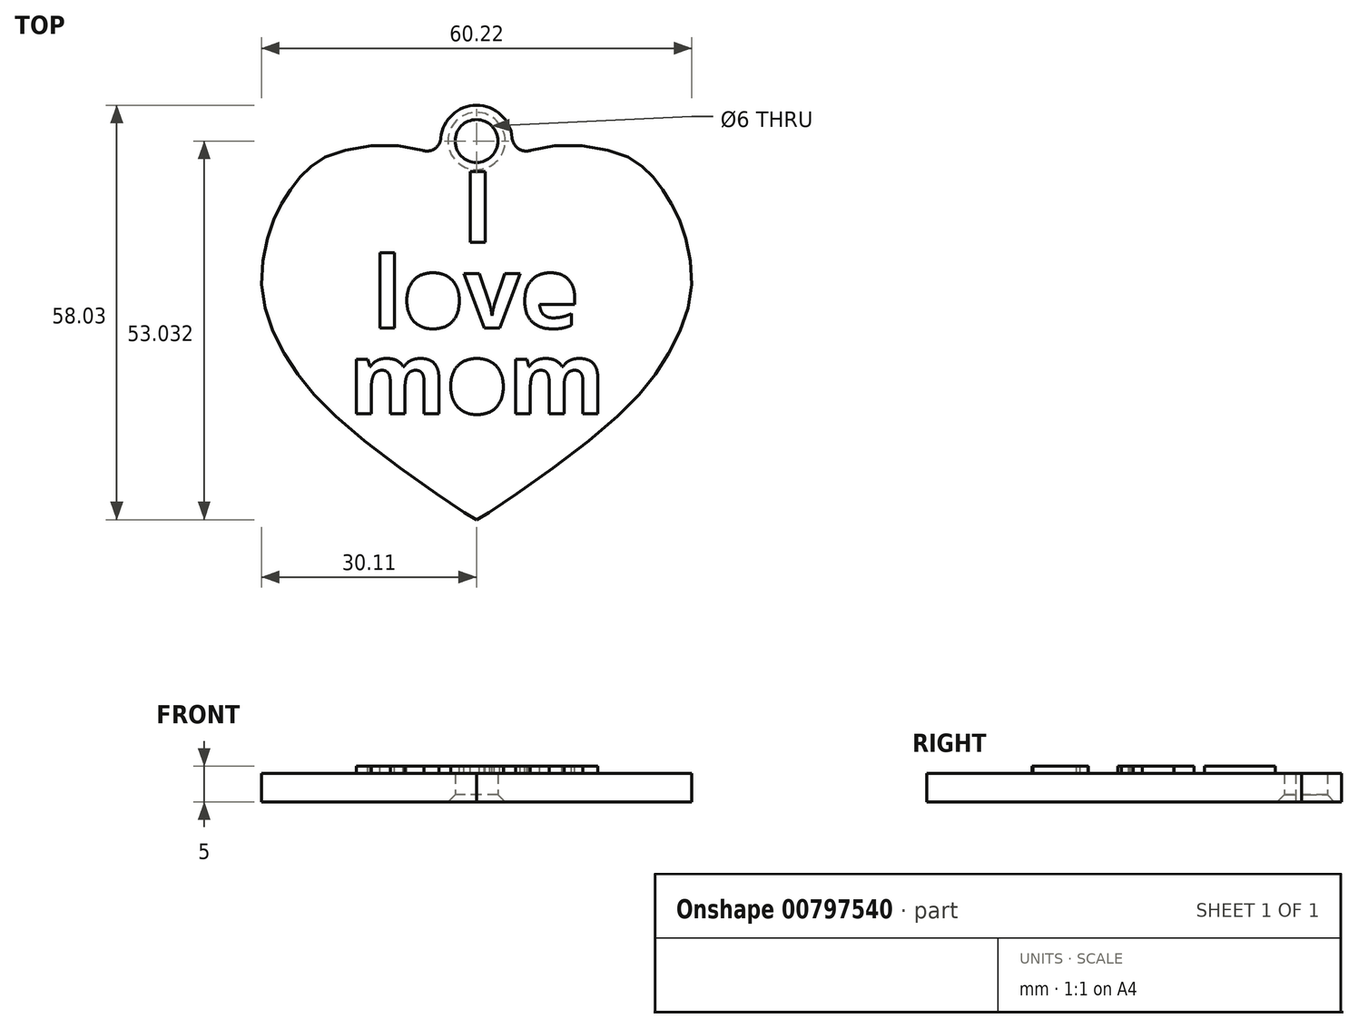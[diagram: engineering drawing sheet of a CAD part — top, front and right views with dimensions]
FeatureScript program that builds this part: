
annotation { "Feature Type Name" : "Feature", "Feature Type Description" : "" }
export const myFeature = defineFeature(function(context is Context, id is Id, definition is map)
    precondition{}
    {
        {
            var Q0;
            Q0=qCreatedBy(makeId("Top.planeOp"),FACE);
            var sketch = newSketch(context, id + "F0", { "sketchPlane" : qUnion([Q0])});
            skArc(sketch, "E0", {"start": v(2.4, 16.93) * mm, "mid": v(0, 26.31) * mm, "end": v(-2.4, 16.93) * mm});
            skCircle(sketch, "E1", {"center": v(0, 21.31) * mm, "radius": 3 * mm});
            skFitSpline(sketch, "E2", {"points": [v(2.4, 16.93) * mm, v(9.1, 20.42) * mm, v(19.97, 19.56) * mm, v(24.06, 16.93) * mm, v(26.63, 13.64) * mm, v(28.97, 8.64) * mm, v(30, 0) * mm, v(26.36, -9.32) * mm, v(16.4, -20.1) * mm, v(0, -31.72) * mm, v(0, -31.66) * mm], "startDerivative": vector(58, 43.33) * mm, "endDerivative": vector(3.18, 9) * mm});
            skFitSpline(sketch, "E3.MirrorCS", {"points": [v(-2.4, 16.93) * mm, v(-9.1, 20.42) * mm, v(-19.97, 19.56) * mm, v(-24.06, 16.93) * mm, v(-26.63, 13.64) * mm, v(-28.97, 8.64) * mm, v(-30, 0) * mm, v(-26.36, -9.32) * mm, v(-16.4, -20.1) * mm, v(0, -31.72) * mm, v(0, -31.66) * mm], "startDerivative": vector(-58, 43.33) * mm, "endDerivative": vector(-3.18, 9) * mm});
            skSolve(sketch);
        }
        {
            var Q0;
            Q0 = qSketchRegion(id + "F0", true);
            extrude(context, id + "F1", {"entities" : qUnion([Q0]), "depth" : 5 * mm, "offsetDistance" : 25 * mm});
        }
        {
            var Q0;
            Q0=makeQuery(id+"F1.opExtrude","SWEPT_EDGE",EDGE,{"disambiguationData":[OSD([sQuery(id+"F0.wireOp",EDGE,"E0"),sQuery(id+"F0.wireOp",EDGE,"E2")])]});
            var Q1;
            Q1=makeQuery(id+"F1.opExtrude","SWEPT_EDGE",EDGE,{"disambiguationData":[OSD([sQuery(id+"F0.wireOp",EDGE,"E0"),sQuery(id+"F0.wireOp",EDGE,"E3.MirrorCS")])]});
            fillet(context, id + "F2", {"entities" : qUnion([Q0, Q1]), "radius" : 2 * mm, "tangentPropagation" : true, "allowEdgeOverflow" : false});
        }
        {
            var Q0;
            Q0=makeQuery(id+"F1.opExtrude","CAP_FACE",FACE,{"disambiguationData":[OSD([sQuery(id+"F0.wireOp",EDGE,"E0"),sQuery(id+"F0.wireOp",EDGE,"E1"),sQuery(id+"F0.wireOp",EDGE,"E2"),sQuery(id+"F0.wireOp",EDGE,"E3.MirrorCS")])],"isStart":false});
            var sketch = newSketch(context, id + "F3", { "sketchPlane" : qUnion([Q0])});
            skText(sketch, "E4", { "text": "I", "fontName": "OpenSans-Bold.ttf"});
            skText(sketch, "E5", { "text": "love", "fontName": "OpenSans-Bold.ttf"});
            skText(sketch, "E6", { "text": "mom", "fontName": "OpenSans-Bold.ttf"});
            const initialGuessF3  = {"E4": [-0.00213, 0.00714, 1, 0, 0.01], "E5": [-0.01462, -0.00486, 1, 0, 0.01], "E6": [-0.01787, -0.01686, 1, 0, 0.01]};
            skSetInitialGuess(sketch, initialGuessF3);
            skSolve(sketch);
        }
        {
            var Q0;
            Q0=makeQuery(id+"F3.imprint","IMPRINT",FACE,{"disambiguationData":[TD([[makeQuery(id+"F3.imprint","IMPRINT",EDGE,{"derivedFrom":sQuery(id+"F3.wireOp",EDGE,"E4.sketch_text.stroke-0")}),1.0]])]});
            extrude(context, id + "F4", {"entities" : qUnion([Q0]), "operationType" : NewBodyOperationType.REMOVE, "oppositeDirection" : true, "depth" : 1 * mm, "offsetDistance" : 25 * mm});
        }
        {
            var Q0;
            Q0=makeQuery(id+"F4.boolean.opBoolean","COPY",EDGE,{"derivedFrom":makeQuery(id+"F4.opExtrude","CAP_EDGE",EDGE,{"disambiguationData":[OSD([sQuery(id+"F0.wireOp",EDGE,"E1")])],"isStart":false})});
            var Q1;
            Q1=makeQuery(id+"F1.opExtrude","CAP_EDGE",EDGE,{"disambiguationData":[OSD([sQuery(id+"F0.wireOp",EDGE,"E1")])],"isStart":true});
            chamfer(context, id + "F5", {"entities" : qUnion([Q0, Q1]), "width" : 1 * mm, "tangentPropagation" : true});
        }
    });
